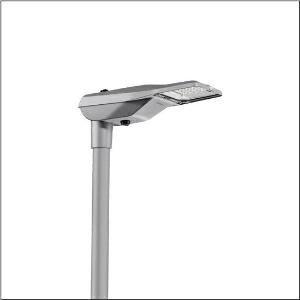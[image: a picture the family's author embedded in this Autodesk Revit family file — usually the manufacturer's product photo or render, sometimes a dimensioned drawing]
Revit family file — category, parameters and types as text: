
# Revit family: streetlight_sl_21_iq_micro___st1_0a_5xe1d51y08cb_5320
name_source: partatom
category: Lighting Fixtures
units: mm (PartAtom-declared; Revit-internal decimal feet)

## family parameters
Cut with Voids When Loaded = No
Host = Face
Light Source = No
Part Type = Normal
Room Calculation Point = No
Round Connector Dimension = Use Diameter
Shared = No

## types (1)
- --- (1 x LED, 2530 lm, 19.1 W, 3000K)
    Apparent Load = 19 VA
    CIE Flux Codes = 37 72 97 100 100
    Color Rendering = 80
    Color Temperature = 3000K
    Default Elevation = 1800 mm
    Description = Streetlight SL 21 iQ micro, mast luminaire, primary light control with lens, of PMMA, primary optical cover: cover, of toughened safety glass, transparent, light distribution: ST1.0a, light emission: direct distribution, primary light characteristic: asymmetric, installation type: post-top, side-entry, LED, High Power LED, rated luminous flux: 2.530lm, luminous efficacy: 133lm/W, light colour: 830, colour temperature: 3000K, control: presetting dimming logarithmic, Street-Remote, Auto-Match, Temp-Guard, Lumen-Switch, Night-Set, Smart-Wire, Light-Fading, Desk-Remote (wireless, voltage-free reading and setting of iQ features in the workshop via application-optimized NFC function/RFID function), optimised constant luminous flux control (CLO 2.0), mains connection: 220..240V, AC, 50/60Hz, start of lifetime: 19W, end of service life: 20W, reduction: 9W, luminaire housing, of diecast aluminium, powder-coated, Siteco® metallic grey (DB 702S), corrosivity category C5 mid according to DIN EN ISO 12944, please order mast flange separately, inclination adjustable: 0°, 5°, 10°, 15°, sealing non-destructively replaceable, multi-level sealing system, length: 528mm, width: 235mm, height: 110mm, mast flange for spigot size: 42mm (side-entry): 5XC10008XM4, 60/48mm (side-entry/post-top): 5XC10108XM2, 76/60mm (side-entry/post-top): 5XC10108XM1, Smart Interface below and above, protection rating (complete): IP66, insulation class (complete): insulation class II (safety insulation), certification: CE, ENEC, ENEC+, VDE, impact resistance: IK09, permissible operating ambient temperature for outdoor applications: -40..+50°C, standard-compliant lighting for roads and squares, packaging unit: 1 piece

Light Distribution: ST1.0a
    Height = 110 mm
    Lamp = 1 x LED
    Lamp Light Flux = 2530 lm
    Lamp Power = 19.1 W
    Lamp count = 1
    Length = 528 mm
    Luminous efficacy = 132 lm/W
    Manufacturer = Siteco
    ModVariant = No
    Model = 5XE1D51Y08CB
    Number of Poles = 1
    OnlyDefault = Yes
    Power Factor = 1
    Product Name = Streetlight SL 21 iQ micro | ST1.0a
    Product group = mast luminaire | pylon top
    ProductGroupID = 6100
    Protection Class = Protection class II
    Protection Degree = IP 66
    RLX_Detail_Level = 1
    RLX_Emergency_Light_Flux = 0 lm
    RLX_Emergency_Type = 0
    RLX_Emergency_Type_DB = No
    RlxData = <blob elided: 98801 chars, md5=fdd82aa4>
    Socket = socket
    Standby Power = 0 W
    System Light Flux = 2530 lm
    System Power = 19 W
    Type Comments = factory setting: luminous flux: 100 % | dim-lin: 254 | 387 mA
    Type Image = l_1007239.jpg
    URL = http://relux.com
    VarID = @adj_045419
    Voltage = 0 V
    Weight = 0.00 kg
    Width = 235 mm

## geometry (parser evidence)
native form markers: Blend x4, Sweep x13
no freeform markers — native parametric forms only
